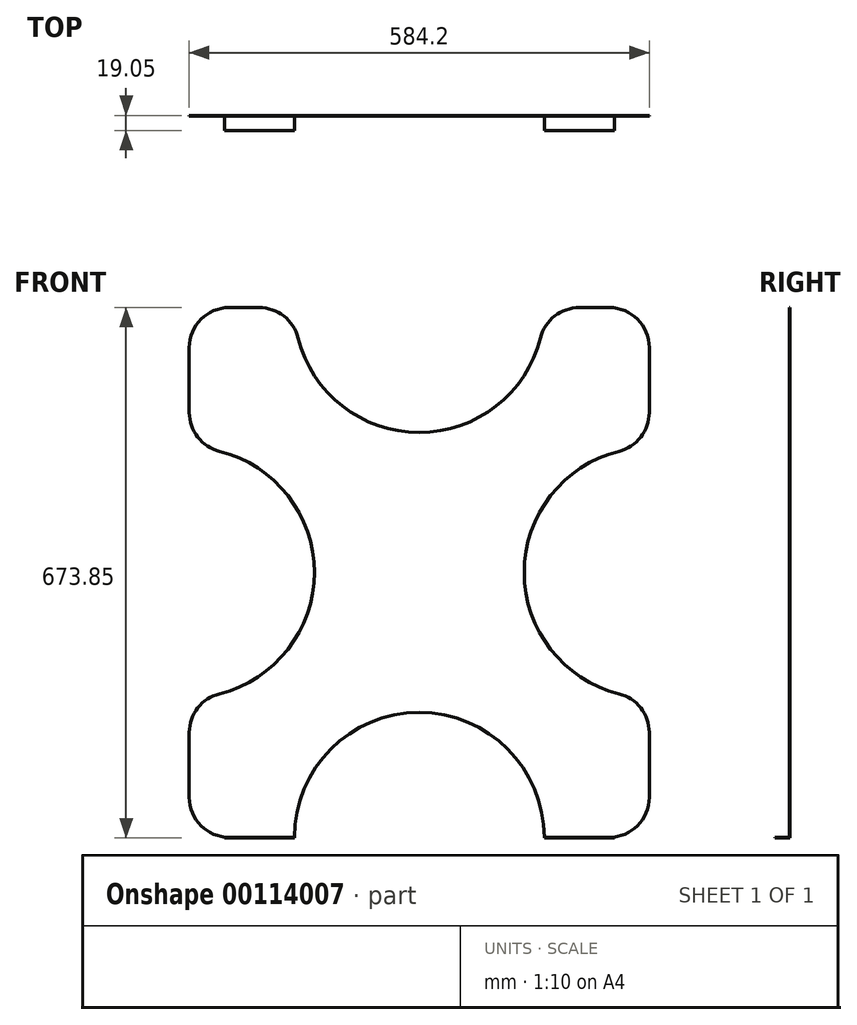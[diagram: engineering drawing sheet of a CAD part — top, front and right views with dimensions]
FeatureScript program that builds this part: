
annotation { "Feature Type Name" : "Feature", "Feature Type Description" : "" }
export const myFeature = defineFeature(function(context is Context, id is Id, definition is map)
    precondition{}
    {
        {
            assignVariable(context, id + "F0", {"name" : "thickness", "anyValue" : 3 / 4});
        }
        {
            var Q0;
            Q0=qCreatedBy(makeId("Front.planeOp"),FACE);
            var sketch = newSketch(context, id + "F1", { "sketchPlane" : qUnion([Q0])});
            skLineSegment(sketch, "E0.bottom", {"start": v(-292.1, 336.55) * mm, "end": v(292.1, 336.55) * mm});
            skLineSegment(sketch, "E0.top", {"start": v(-292.1, -336.55) * mm, "end": v(292.1, -336.55) * mm});
            skLineSegment(sketch, "E0.left", {"start": v(-292.1, 336.55) * mm, "end": v(-292.1, -336.55) * mm});
            skLineSegment(sketch, "E0.right", {"start": v(292.1, 336.55) * mm, "end": v(292.1, -336.55) * mm});
            skPoint(sketch, "E1", {"position": v(0, 336.55) * mm});
            skPoint(sketch, "E2", {"position": v(-292.1, 0) * mm});
            skLineSegment(sketch, "E3", {"start": v(0, 0) * mm, "end": v(-292.1, 0) * mm, "construction": true});
            skLineSegment(sketch, "E4", {"start": v(0, 0) * mm, "end": v(0, 336.55) * mm, "construction": true});
            skCircle(sketch, "E5", {"center": v(-292.1, 0) * mm, "radius": 158.75 * mm});
            skCircle(sketch, "E6.MirrorC", {"center": v(292.1, 0) * mm, "radius": 158.75 * mm});
            skCircle(sketch, "E7", {"center": v(0, 336.55) * mm, "radius": 158.75 * mm});
            skCircle(sketch, "E8.MirrorC", {"center": v(0, -336.55) * mm, "radius": 158.75 * mm});
            skSolve(sketch);
        }
        {
            var Q0;
            {var subQ4=sQuery(id+"F1.wireOp",EDGE,"E0.left");var subQ11=sQuery(id+"F1.wireOp",EDGE,"E0.bottom");var subQ12=makeQuery(id+"F1.imprint","INTERSECT",VERTEX,{"derivedFrom":[subQ11,subQ4]});Q0=makeQuery(id+"F1.imprint","IMPRINT",FACE,{"disambiguationData":[TD([[makeQuery(id+"F1.imprint","IMPRINT",EDGE,{"disambiguationData":[TD([[subQ12,-1.0]])],"derivedFrom":subQ11}),-1.0]])]});}
            extrude(context, id + "F2", {"entities" : qUnion([Q0]), "depth" : (getVariable(context, 'thickness')) * mm});
        }
        {
            var Q0;
            {var subQ0=sQuery(id+"F1.wireOp",EDGE,"E7");var subQ1=sQuery(id+"F1.wireOp",EDGE,"E0.bottom");Q0=makeQuery(id+"F2.opExtrude","SWEPT_EDGE",EDGE,{"disambiguationData":[OSD([subQ1,subQ0]),TDD([makeQuery(id+"F1.imprint","INTERSECT",VERTEX,{"disambiguationData":[OD(1.0)],"derivedFrom":[subQ1,subQ0]})])]});}
            var Q1;
            {var subQ0=sQuery(id+"F1.wireOp",EDGE,"E7");var subQ1=sQuery(id+"F1.wireOp",EDGE,"E0.bottom");Q1=makeQuery(id+"F2.opExtrude","SWEPT_EDGE",EDGE,{"disambiguationData":[OSD([subQ1,subQ0]),TDD([makeQuery(id+"F1.imprint","INTERSECT",VERTEX,{"disambiguationData":[OD(0.0)],"derivedFrom":[subQ1,subQ0]})])]});}
            var Q2;
            {var subQ0=sQuery(id+"F1.wireOp",EDGE,"E6.MirrorC");var subQ1=sQuery(id+"F1.wireOp",EDGE,"E0.right");Q2=makeQuery(id+"F2.opExtrude","SWEPT_EDGE",EDGE,{"disambiguationData":[OSD([subQ1,subQ0]),TDD([makeQuery(id+"F1.imprint","INTERSECT",VERTEX,{"disambiguationData":[OD(0.0)],"derivedFrom":[subQ1,subQ0]})])]});}
            var Q3;
            {var subQ0=sQuery(id+"F1.wireOp",EDGE,"E6.MirrorC");var subQ1=sQuery(id+"F1.wireOp",EDGE,"E0.right");Q3=makeQuery(id+"F2.opExtrude","SWEPT_EDGE",EDGE,{"disambiguationData":[OSD([subQ1,subQ0]),TDD([makeQuery(id+"F1.imprint","INTERSECT",VERTEX,{"disambiguationData":[OD(1.0)],"derivedFrom":[subQ1,subQ0]})])]});}
            var Q4;
            {var subQ0=sQuery(id+"F1.wireOp",EDGE,"E5");var subQ1=sQuery(id+"F1.wireOp",EDGE,"E0.left");Q4=makeQuery(id+"F2.opExtrude","SWEPT_EDGE",EDGE,{"disambiguationData":[OSD([subQ1,subQ0]),TDD([makeQuery(id+"F1.imprint","INTERSECT",VERTEX,{"disambiguationData":[OD(1.0)],"derivedFrom":[subQ1,subQ0]})])]});}
            var Q5;
            {var subQ0=sQuery(id+"F1.wireOp",EDGE,"E5");var subQ1=sQuery(id+"F1.wireOp",EDGE,"E0.left");Q5=makeQuery(id+"F2.opExtrude","SWEPT_EDGE",EDGE,{"disambiguationData":[OSD([subQ1,subQ0]),TDD([makeQuery(id+"F1.imprint","INTERSECT",VERTEX,{"disambiguationData":[OD(0.0)],"derivedFrom":[subQ1,subQ0]})])]});}
            var Q6;
            Q6=makeQuery(id+"F2.opExtrude","SWEPT_EDGE",EDGE,{"disambiguationData":[OSD([sQuery(id+"F1.wireOp",EDGE,"E0.top"),sQuery(id+"F1.wireOp",EDGE,"E0.right")])]});
            var Q7;
            Q7=makeQuery(id+"F2.opExtrude","SWEPT_EDGE",EDGE,{"disambiguationData":[OSD([sQuery(id+"F1.wireOp",EDGE,"E0.top"),sQuery(id+"F1.wireOp",EDGE,"E0.left")])]});
            var Q8;
            Q8=makeQuery(id+"F2.opExtrude","SWEPT_EDGE",EDGE,{"disambiguationData":[OSD([sQuery(id+"F1.wireOp",EDGE,"E0.bottom"),sQuery(id+"F1.wireOp",EDGE,"E0.right")])]});
            var Q9;
            Q9=makeQuery(id+"F2.opExtrude","SWEPT_EDGE",EDGE,{"disambiguationData":[OSD([sQuery(id+"F1.wireOp",EDGE,"E0.bottom"),sQuery(id+"F1.wireOp",EDGE,"E0.left")])]});
            fillet(context, id + "F3", {"entities" : qUnion([Q0, Q1, Q2, Q3, Q4, Q5, Q6, Q7, Q8, Q9]), "radius" : 50.8 * mm, "tangentPropagation" : true, "allowEdgeOverflow" : false});
        }
        {
            var Q0;
            {var subQ0=sQuery(id+"F1.wireOp",EDGE,"E0.top");Q0=makeQuery(id+"F2.opExtrude","SWEPT_FACE",FACE,{"disambiguationData":[OSD([subQ0]),TDD([makeQuery(id+"F1.imprint","IMPRINT",EDGE,{"disambiguationData":[TD([[makeQuery(id+"F1.imprint","INTERSECT",VERTEX,{"derivedFrom":[subQ0,sQuery(id+"F1.wireOp",EDGE,"E0.left")]}),-1.0]])],"derivedFrom":subQ0})])]});}
            var sketch = newSketch(context, id + "F4", { "sketchPlane" : qUnion([Q0])});
            skLineSegment(sketch, "E9.bottom", {"start": v(-158.75, 19.05) * mm, "end": v(-247.65, 19.05) * mm});
            skLineSegment(sketch, "E9.top", {"start": v(-158.75, 0) * mm, "end": v(-247.65, 0) * mm});
            skLineSegment(sketch, "E9.left", {"start": v(-158.75, 19.05) * mm, "end": v(-158.75, 0) * mm});
            skLineSegment(sketch, "E9.right", {"start": v(-247.65, 19.05) * mm, "end": v(-247.65, 0) * mm});
            skLineSegment(sketch, "E10.bottom", {"start": v(158.75, 19.05) * mm, "end": v(247.65, 19.05) * mm});
            skLineSegment(sketch, "E10.top", {"start": v(158.75, 0) * mm, "end": v(247.65, 0) * mm});
            skLineSegment(sketch, "E10.left", {"start": v(158.75, 19.05) * mm, "end": v(158.75, 0) * mm});
            skLineSegment(sketch, "E10.right", {"start": v(247.65, 19.05) * mm, "end": v(247.65, 0) * mm});
            skSolve(sketch);
        }
        {
            var Q0;
            Q0 = qSketchRegion(id + "F4", true);
            extrude(context, id + "F5", {"entities" : qUnion([Q0]), "operationType" : NewBodyOperationType.ADD, "depth" : (getVariable(context, 'thickness')) * mm});
        }
    });
